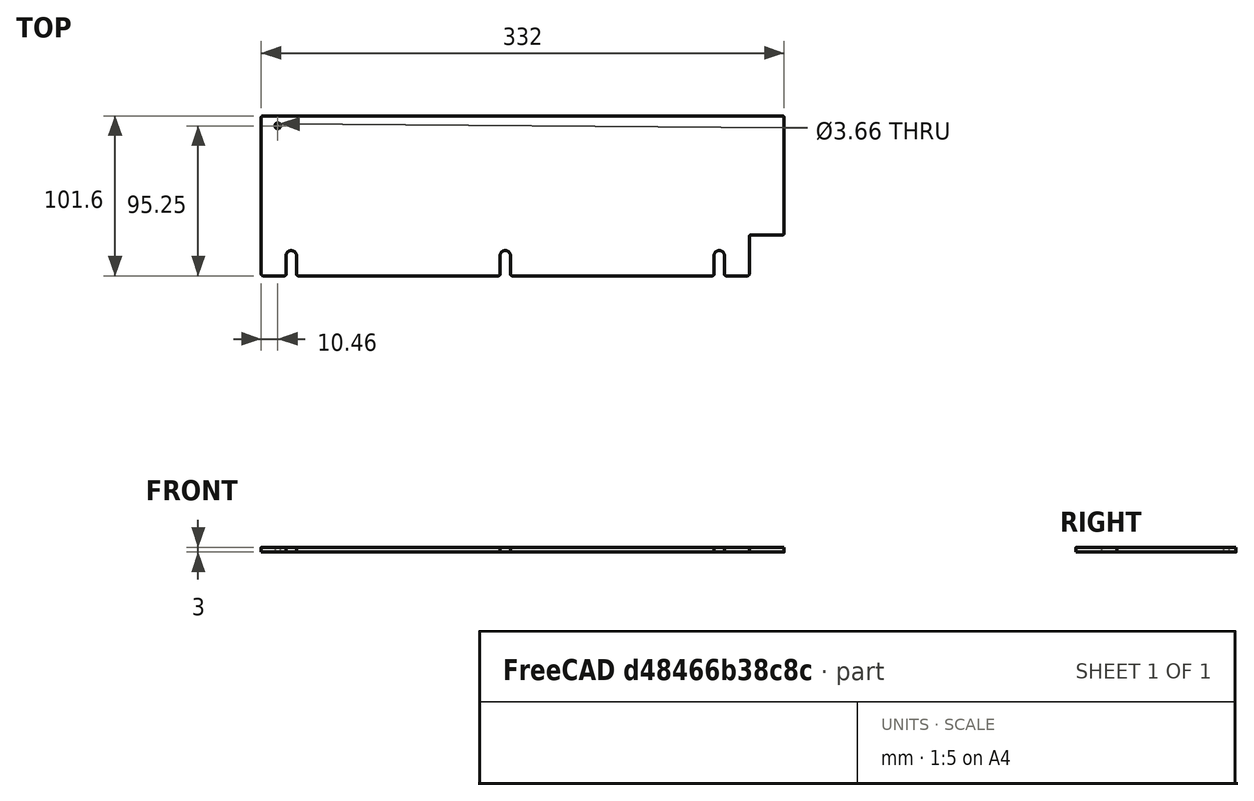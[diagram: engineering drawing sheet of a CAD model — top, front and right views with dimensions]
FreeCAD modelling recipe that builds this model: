
FCSTD DOCUMENT  (FreeCAD 0.21R33675 (Git))
Label: right_wall_back
License: All rights reserved
LicenseURL: http://en.wikipedia.org/wiki/All_rights_reserved
objects: Spreadsheet::Sheet×1, Sketcher::SketchObject×1, PartDesign::Pad×1, PartDesign::Body×1
note: 4 computed .brp shape members not serialized (recipe doc carries the construction recipe); baked Part::Feature solids carry a one-line shape summary decoded from their .brp

FEATURE [Spreadsheet::Sheet] Spreadsheet
  cells = A2='Parameters; A3='Thickness; B3(Thickness)==3 mm; A4='BeamLength; B4(BeamLength)==18 in; A5='BracketLength; B5(BracketLength)==108.6 mm; A6='DistanceLeftBracketEdgeToDoor; B6(DistanceLeftBracketEdgeToDoor)==82.4999 mm; A7='DistanceRightBracketEdgeToDoor; B7(DistanceRightBracketEdgeToDoor)==23.1001 mm; A8='ServoOffsetFromCenter; B8(ServoOffsetFromCenter)==3 in + 1 * (DistanceLeftBracketEdgeToDoor - DistanceRightBracketEdgeToDoor); A9='DoorMargin; B9(DoorMargin)==1 mm; A10='LengthMargin; B10(LengthMargin)==0 mm; A11='LengthLeftBracketEdgeToDoorGap; B11(LengthLeftBracketEdgeToDoorGap)==DistanceLeftBracketEdgeToDoor - DoorMargin; A12='LengthRightBracketEdgeToDoorGap; B12(LengthRightBracketEdgeToDoorGap)==DistanceRightBracketEdgeToDoor - DoorMargin; A13='LengthDoorGap; B13(LengthDoorGap)==BracketLength - LengthLeftBracketEdgeToDoorGap - LengthRightBracketEdgeToDoorGap; A14='BeamLengthMinusBracketLength; B14(BeamLengthMinusBracketLength)==BeamLength - BracketLength; A15='DistanceBackToDoor; B15(DistanceBackToDoor)==0.5 * BeamLengthMinusBracketLength + LengthRightBracketEdgeToDoorGap + ServoOffsetFromCenter; A16='DistanceBackToBracket; B16(DistanceBackToBracket)==0.5 * BeamLengthMinusBracketLength + ServoOffsetFromCenter; A17='LengthBackToDoor; B17(LengthBackToDoor)==DistanceBackToDoor - LengthMargin; A18='LengthBackToBracket; B18(LengthBackToBracket)==DistanceBackToBracket - LengthMargin; A19='Height; B19(Height)==4 in; A21='CutoutMargin; B21(CutoutMargin)==0.5 mm; A22='CutoutHeight; B22(CutoutHeight)==1 in + CutoutMargin; A23='FilletRadius; B23(FilletRadius)==1 mm; A24='MountHoleDiameter; B24(MountHoleDiameter)==0.26 in; A25='MountHoleDistanceFromBottom; B25(MountHoleDistanceFromBottom)==0.5 in; A26='MountHoleSideMargin; B26(MountHoleSideMargin)==0.75 in; A28='RABracketWidth; B28(RABracketWidth)==0.5 in; A29='RABracketHoleDiameter; B29(RABracketHoleDiameter)==0.144 in; A30='RABracketHoleOffset; B30(RABracketHoleOffset)==0.412 in; A31='RAUpperBracketHoleFromTop; B31(RAUpperBracketHoleFromTop)==0.5 * RABracketWidth; A32='RABracketHoleFromSide; B32(RABracketHoleFromSide)==RABracketHoleOffset; B38==3 in + DistanceLeftBracketEdgeToDoor + 0.5 * Thickness - 0.5 * BracketLength
FEATURE [Sketcher::SketchObject] Sketch
  FullyConstrained = true
  MapMode = 5
  Support = -> [XY_Plane]
  expr: Constraints[101] = Spreadsheet.RAUpperBracketHoleFromTop
  expr: Constraints[103] = Spreadsheet.RABracketHoleDiameter
  expr: Constraints[14] = Spreadsheet.FilletRadius
  expr: Constraints[20] = Spreadsheet.Height
  expr: Constraints[43] = Spreadsheet.MountHoleDistanceFromBottom
  expr: Constraints[44] = Spreadsheet.MountHoleDiameter
  expr: Constraints[59] = Spreadsheet.MountHoleSideMargin
  expr: Constraints[7] = Spreadsheet.LengthBackToDoor
  expr: Constraints[8] = Spreadsheet.LengthBackToBracket
  expr: Constraints[9] = Spreadsheet.CutoutHeight
  sketch-geometry (54):
    g0: LineSegment StartX=0 StartY=100.6 StartZ=0 EndX=0 EndY=1 EndZ=0
    g1: LineSegment StartX=1 StartY=0 StartZ=0 EndX=308.9 EndY=0 EndZ=0
    g2: LineSegment StartX=309.9 StartY=1 StartZ=0 EndX=309.9 EndY=24.9 EndZ=0
    g3: LineSegment StartX=310.9 StartY=25.9 StartZ=0 EndX=331 EndY=25.9 EndZ=0
    g4: LineSegment StartX=332 StartY=26.9 StartZ=0 EndX=332 EndY=100.6 EndZ=0
    g5: LineSegment StartX=331 StartY=101.6 StartZ=0 EndX=1 EndY=101.6 EndZ=0
    g6: ArcOfCircle CenterX=1 CenterY=100.6 CenterZ=0 NormalX=0 NormalY=0 NormalZ=1 AngleXU=0 Radius=1 StartAngle=1.5708 EndAngle=3.14159
    g7: GeomPoint X=0 Y=101.6 Z=0
    g8: ArcOfCircle CenterX=1 CenterY=1 CenterZ=0 NormalX=0 NormalY=0 NormalZ=1 AngleXU=0 Radius=1 StartAngle=3.14159 EndAngle=4.71239
    g9: GeomPoint X=0 Y=0 Z=0
    g10: ArcOfCircle CenterX=308.9 CenterY=1 CenterZ=0 NormalX=0 NormalY=0 NormalZ=1 AngleXU=0 Radius=1 StartAngle=4.71239 EndAngle=6.28319
    g11: GeomPoint X=309.9 Y=0 Z=0
    g12: ArcOfCircle CenterX=310.9 CenterY=24.9 CenterZ=0 NormalX=0 NormalY=0 NormalZ=1 AngleXU=0 Radius=1 StartAngle=1.5708 EndAngle=3.14159
    g13: GeomPoint X=309.9 Y=25.9 Z=0
    g14: ArcOfCircle CenterX=331 CenterY=26.9 CenterZ=0 NormalX=0 NormalY=0 NormalZ=1 AngleXU=0 Radius=1 StartAngle=4.71239 EndAngle=6.28319
    g15: GeomPoint X=332 Y=25.9 Z=0
    g16: ArcOfCircle CenterX=331 CenterY=100.6 CenterZ=0 NormalX=0 NormalY=0 NormalZ=1 AngleXU=0 Radius=1 StartAngle=1.061e-13 EndAngle=1.5708
    g17: GeomPoint X=332 Y=101.6 Z=0
    g18: GeomPoint X=19.05 Y=0 Z=0
    g19: LineSegment StartX=19.05 StartY=0 StartZ=0 EndX=19.05 EndY=12.7 EndZ=0
    g20: Circle CenterX=19.05 CenterY=12.7 CenterZ=0 NormalX=0 NormalY=0 NormalZ=1 AngleXU=0 Radius=3.302
    g21: LineSegment StartX=290.85 StartY=12.7 StartZ=0 EndX=290.85 EndY=0 EndZ=0
    g22: LineSegment StartX=290.85 StartY=12.7 StartZ=0 EndX=309.9 EndY=12.7 EndZ=0
    g23: LineSegment StartX=19.05 StartY=12.7 StartZ=0 EndX=0 EndY=12.7 EndZ=0
    g24: Circle CenterX=290.85 CenterY=12.7 CenterZ=0 NormalX=0 NormalY=0 NormalZ=1 AngleXU=0 Radius=3.302
    g25: ArcOfCircle CenterX=19.05 CenterY=12.7 CenterZ=0 NormalX=0 NormalY=0 NormalZ=1 AngleXU=0 Radius=3.302 StartAngle=0 EndAngle=3.14159
    g26: LineSegment StartX=19.05 StartY=12.7 StartZ=0 EndX=22.352 EndY=12.7 EndZ=0
    g27: LineSegment StartX=15.748 StartY=12.7 StartZ=0 EndX=15.748 EndY=1 EndZ=0
    g28: LineSegment StartX=22.352 StartY=12.7 StartZ=0 EndX=22.352 EndY=1 EndZ=0
    g29: ArcOfCircle CenterX=14.748 CenterY=1 CenterZ=0 NormalX=0 NormalY=0 NormalZ=1 AngleXU=0 Radius=1 StartAngle=4.71239 EndAngle=6.28319
    g30: ArcOfCircle CenterX=23.352 CenterY=1 CenterZ=0 NormalX=0 NormalY=0 NormalZ=1 AngleXU=0 Radius=1 StartAngle=3.14159 EndAngle=4.71239
    g31: ArcOfCircle CenterX=290.85 CenterY=12.7 CenterZ=0 NormalX=0 NormalY=0 NormalZ=1 AngleXU=0 Radius=3.302 StartAngle=-1.8e-15 EndAngle=3.14159
    g32: LineSegment StartX=290.85 StartY=12.7 StartZ=0 EndX=287.548 EndY=12.7 EndZ=0
    g33: LineSegment StartX=287.548 StartY=12.7 StartZ=0 EndX=287.548 EndY=1 EndZ=0
    g34: LineSegment StartX=294.152 StartY=12.7 StartZ=0 EndX=294.152 EndY=1 EndZ=0
    g35: ArcOfCircle CenterX=286.548 CenterY=1 CenterZ=0 NormalX=0 NormalY=0 NormalZ=1 AngleXU=0 Radius=1 StartAngle=4.71239 EndAngle=6.28319
    g36: ArcOfCircle CenterX=295.152 CenterY=1 CenterZ=0 NormalX=0 NormalY=0 NormalZ=1 AngleXU=0 Radius=1 StartAngle=3.14159 EndAngle=4.71239
    g37: LineSegment StartX=295.152 StartY=0 StartZ=0 EndX=308.9 EndY=0 EndZ=0
    g38: LineSegment StartX=1 StartY=0 StartZ=0 EndX=14.748 EndY=0 EndZ=0
    g39: LineSegment StartX=0 StartY=101.6 StartZ=0 EndX=10.46 EndY=101.6 EndZ=0
    g40: LineSegment StartX=10.46 StartY=101.6 StartZ=0 EndX=10.46 EndY=95.25 EndZ=0
    g41: Circle CenterX=10.46 CenterY=95.25 CenterZ=0 NormalX=0 NormalY=0 NormalZ=1 AngleXU=0 Radius=1.8288
    g42: GeomPoint X=154.95 Y=0 Z=0
    g43: LineSegment StartX=154.95 StartY=0 StartZ=0 EndX=154.95 EndY=12.7 EndZ=0
    g44: LineSegment StartX=151.648 StartY=12.7 StartZ=0 EndX=158.252 EndY=12.7 EndZ=0
    g45: ArcOfCircle CenterX=154.95 CenterY=12.7 CenterZ=0 NormalX=0 NormalY=0 NormalZ=1 AngleXU=0 Radius=3.302 StartAngle=0 EndAngle=3.14159
    g46: LineSegment StartX=151.648 StartY=12.7 StartZ=0 EndX=151.648 EndY=1 EndZ=0
    g47: LineSegment StartX=158.252 StartY=12.7 StartZ=0 EndX=158.252 EndY=1 EndZ=0
    g48: LineSegment StartX=23.352 StartY=0 StartZ=0 EndX=150.648 EndY=0 EndZ=0
    g49: LineSegment StartX=159.252 StartY=0 StartZ=0 EndX=286.548 EndY=0 EndZ=0
    g50: ArcOfCircle CenterX=150.648 CenterY=1 CenterZ=0 NormalX=0 NormalY=0 NormalZ=1 AngleXU=0 Radius=1 StartAngle=4.71239 EndAngle=6.28319
    g51: GeomPoint X=151.648 Y=0 Z=0
    g52: ArcOfCircle CenterX=159.252 CenterY=1 CenterZ=0 NormalX=0 NormalY=0 NormalZ=1 AngleXU=0 Radius=1 StartAngle=3.14159 EndAngle=4.71239
    g53: GeomPoint X=158.252 Y=0 Z=0
  constraints (130):
    c: Vertical(g0)
    c: Horizontal(g1)
    c: Vertical(g2)
    c: Horizontal(g3)
    c: Vertical(g4)
    c: Horizontal(g5)
    c: Coincident(g-1,g9)
    c: DistanceX(g7,g17) = 332
    c: DistanceX(g9,g11) = 309.9
    c: DistanceY(g11,g13) = 25.9
    c: PointOnObject(g7,g0)
    c: PointOnObject(g7,g5)
    c: Tangent(g0,g6) = -1.5708
    c: Tangent(g5,g6) = -1.5708
    c: Radius(g6) = 1
    c: PointOnObject(g9,g0)
    c: PointOnObject(g9,g1)
    c: Tangent(g0,g8) = -1.5708
    c: Tangent(g1,g8) = -1.5708
    c: Equal(g8,g6)
    c: DistanceY(g1,g5) = 101.6
    c: PointOnObject(g11,g1)
    c: PointOnObject(g11,g2)
    c: Tangent(g1,g10) = -1.5708
    c: Tangent(g2,g10) = -1.5708
    c: Equal(g10,g8)
    c: PointOnObject(g13,g2)
    c: PointOnObject(g13,g3)
    c: Tangent(g2,g12) = 1.5708
    c: Tangent(g3,g12) = 1.5708
    c: Equal(g12,g10)
    c: PointOnObject(g15,g3)
    c: PointOnObject(g15,g4)
    c: Tangent(g3,g14) = -1.5708
    c: Tangent(g4,g14) = -1.5708
    c: Equal(g14,g12)
    c: PointOnObject(g17,g5)
    c: PointOnObject(g17,g4)
    c: Tangent(g5,g16) = -1.5708
    c: Tangent(g4,g16) = -1.5708
    c: Equal(g16,g14)
    c: Coincident(g19,g18)
    c: Vertical(g19)
    c: DistanceY(g19,g19) = 12.7
    c: Diameter(g20) = 6.604
    c: Coincident(g20,g19)
    c: PointOnObject(g18,g1)
    c: PointOnObject(g21,g1)
    c: Vertical(g21)
    c: Equal(g19,g21)
    c: Coincident(g22,g21)
    c: PointOnObject(g22,g2)
    c: Horizontal(g22)
    c: Coincident(g23,g20)
    c: PointOnObject(g23,g0)
    c: Horizontal(g23)
    c: Equal(g23,g22)
    c: Coincident(g24,g21)
    c: Equal(g24,g20)
    c: DistanceX(g23,g23) = 19.05
    c: Coincident(g25,g19)
    c: PointOnObject(g25,g23)
    c: Coincident(g26,g25)
    c: Coincident(g26,g25)
    c: Horizontal(g26)
    c: PointOnObject(g25,g20)
    c: Coincident(g27,g25)
    c: Vertical(g27)
    c: Coincident(g28,g25)
    c: Vertical(g28)
    c: Equal(g27,g28)
    c: Tangent(g29,g27) = 1.5708
    c: Tangent(g29,g1) = -1.5708
    c: Tangent(g30,g28) = -1.5708
    c: Tangent(g30,g1) = -1.5708
    c: Equal(g29,g8)
    c: Coincident(g31,g21)
    c: PointOnObject(g31,g22)
    c: Coincident(g32,g31)
    c: Coincident(g32,g31)
    c: Horizontal(g32)
    c: PointOnObject(g31,g24)
    c: Coincident(g33,g31)
    c: Vertical(g33)
    c: Coincident(g34,g31)
    c: Vertical(g34)
    c: Equal(g33,g34)
    c: Tangent(g35,g33) = 1.5708
    c: Tangent(g35,g1) = -1.5708
    c: Tangent(g36,g34) = -1.5708
    c: Tangent(g36,g1) = -1.5708
    c: Equal(g36,g10)
    c: Coincident(g37,g36)
    c: Coincident(g37,g10)
    c: Coincident(g38,g8)
    c: Coincident(g38,g29)
    c: Horizontal(g39)
    c: Coincident(g7,g39)
    c: DistanceX(g39,g39) = 10.46
    c: Coincident(g40,g39)
    c: Vertical(g40)
    c: DistanceY(g40,g40) = 6.35
    c: Coincident(g41,g40)
    c: Diameter(g41) = 3.6576
    c: Symmetric(g30,g35,g42)
    c: Coincident(g43,g42)
    c: Vertical(g43)
    c: Symmetric(g44,g44,g43)
    c: Coincident(g45,g44)
    c: Coincident(g45,g44)
    c: Horizontal(g44)
    c: Vertical(g46)
    c: Tangent(g46,g45) = -1.5708
    c: Tangent(g47,g45) = 1.5708
    c: PointOnObject(g51,g1)
    c: PointOnObject(g53,g1)
    c: Coincident(g48,g30)
    c: Coincident(g49,g35)
    c: Equal(g21,g43)
    c: Equal(g25,g45)
    c: PointOnObject(g51,g46)
    c: PointOnObject(g51,g48)
    c: Tangent(g46,g50) = 1.5708
    c: Tangent(g48,g50) = -1.5708
    c: PointOnObject(g53,g47)
    c: PointOnObject(g53,g49)
    c: Tangent(g47,g52) = -1.5708
    c: Tangent(g49,g52) = -1.5708
    c: Equal(g50,g30)
    c: Equal(g52,g35)
FEATURE [PartDesign::Pad] Pad
  Direction = (0,0,1)
  Length = 3
  Length2 = 10
  Profile = -> Sketch
  ReferenceAxis = -> Sketch [N_Axis]
  Type = 0
  expr: Length = Spreadsheet.Thickness
FEATURE [PartDesign::Body] Body
  Group = -> [Sketch,Pad]
  Origin = -> Origin
  Tip = -> Pad
